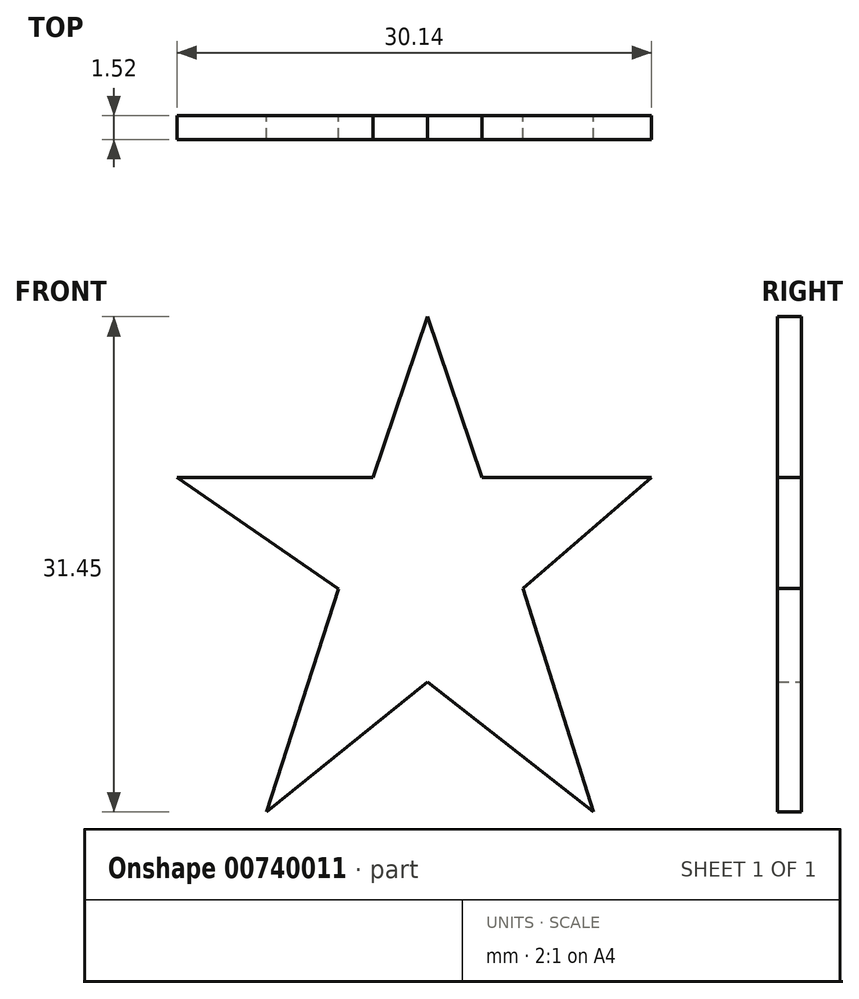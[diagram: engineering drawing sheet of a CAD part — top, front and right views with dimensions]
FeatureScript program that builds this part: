
annotation { "Feature Type Name" : "Feature", "Feature Type Description" : "" }
export const myFeature = defineFeature(function(context is Context, id is Id, definition is map)
    precondition{}
    {
        {
            var Q0;
            Q0=qCreatedBy(makeId("Front.planeOp"),FACE);
            var sketch = newSketch(context, id + "F0", { "sketchPlane" : qUnion([Q0])});
            skCircle(sketch, "E0", {"center": v(0, 0) * mm, "radius": 19.05 * mm});
            skSolve(sketch);
        }
        {
            var Q0;
            Q0=makeQuery(id+"F0.imprint","IMPRINT",FACE,{"disambiguationData":[TD([[makeQuery(id+"F0.imprint","IMPRINT",EDGE,{"derivedFrom":sQuery(id+"F0.wireOp",EDGE,"E0")}),1.0]])]});
            var sketch = newSketch(context, id + "F1", { "sketchPlane" : qUnion([Q0])});
            skLineSegment(sketch, "E1", {"start": v(0, 17.25) * mm, "end": v(3.45, 7.04) * mm});
            skLineSegment(sketch, "E2", {"start": v(3.45, 7.04) * mm, "end": v(14.23, 7.04) * mm});
            skLineSegment(sketch, "E3", {"start": v(14.23, 7.04) * mm, "end": v(6.07, 0) * mm});
            skLineSegment(sketch, "E4", {"start": v(6.07, 0) * mm, "end": v(10.54, -14.2) * mm});
            skLineSegment(sketch, "E5", {"start": v(10.54, -14.2) * mm, "end": v(0, -5.95) * mm});
            skLineSegment(sketch, "E6", {"start": v(0, -5.95) * mm, "end": v(-10.23, -14.2) * mm});
            skLineSegment(sketch, "E7", {"start": v(-10.23, -14.2) * mm, "end": v(-5.66, -0.03) * mm});
            skLineSegment(sketch, "E8", {"start": v(-5.66, -0.03) * mm, "end": v(-15.91, 7.04) * mm});
            skLineSegment(sketch, "E9", {"start": v(-15.91, 7.04) * mm, "end": v(-3.45, 7.04) * mm});
            skLineSegment(sketch, "E10", {"start": v(-3.45, 7.04) * mm, "end": v(0, 17.25) * mm});
            skSolve(sketch);
        }
        {
            var Q0;
            Q0 = qSketchRegion(id + "F1", true);
            extrude(context, id + "F2", {"entities" : qUnion([Q0]), "depth" : 1.52 * mm, "offsetDistance" : 25.4 * mm});
        }
    });
